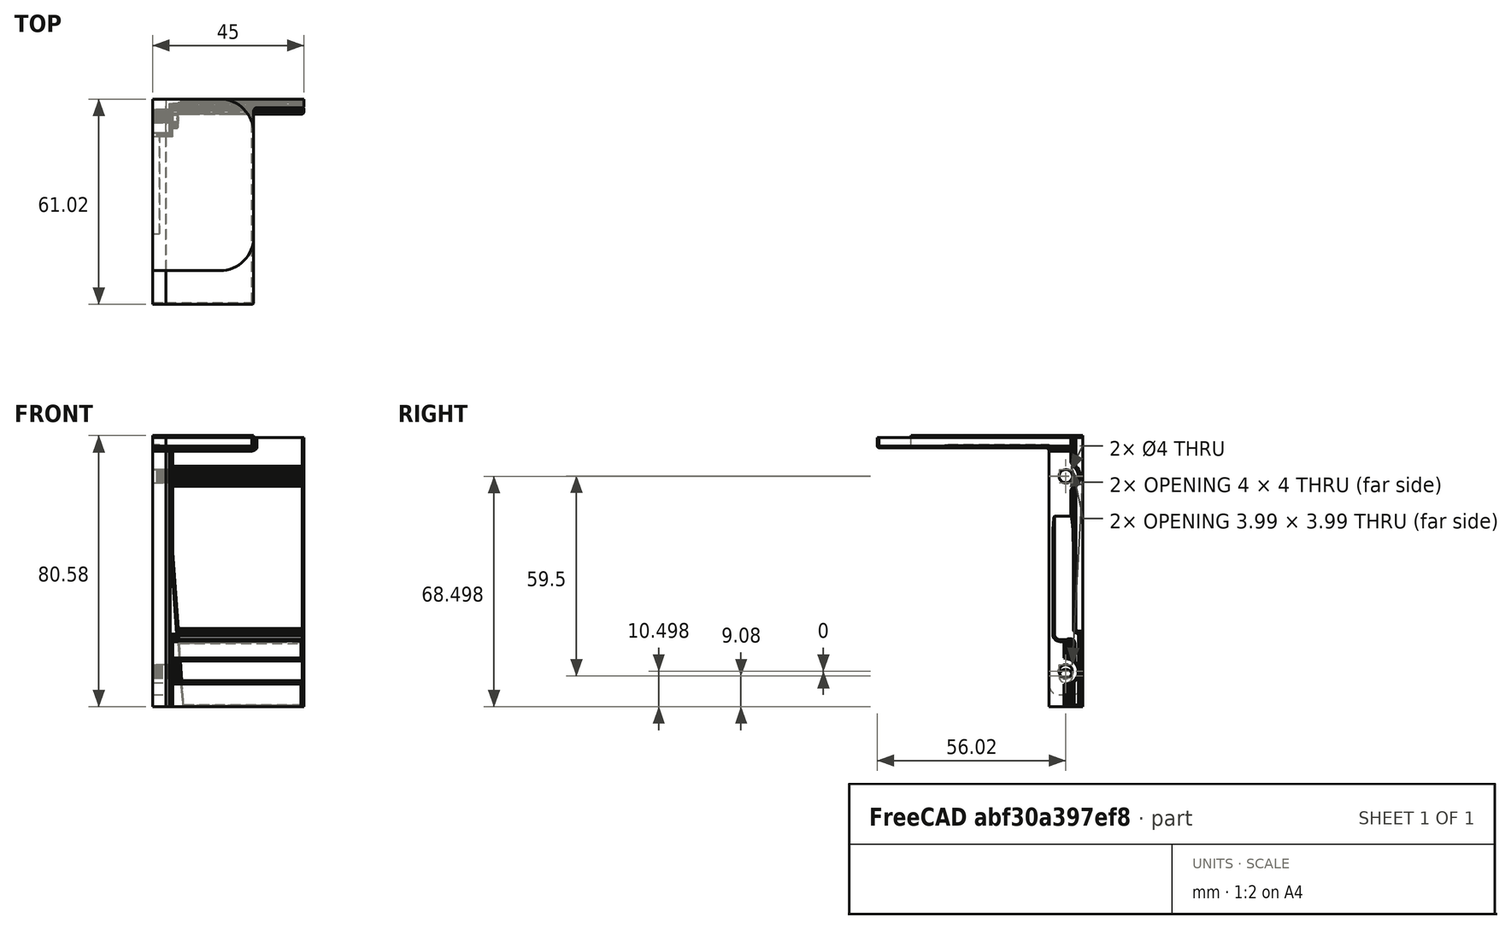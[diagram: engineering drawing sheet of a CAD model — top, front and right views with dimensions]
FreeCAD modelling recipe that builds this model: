
FCSTD DOCUMENT  (FreeCAD 0.19R)
Label: anycubic_max4pro_x_limit
License: All rights reserved
LicenseURL: http://en.wikipedia.org/wiki/All_rights_reserved
objects: Part::Feature×3, Part::FeaturePython×3, Part::Box×2, Part::Fillet×2, Part::Cylinder×2, Part::MultiFuse×2, App::Part×1, Mesh::Feature×1, Part::Refine×1, Part::Plane×1, App::DocumentObjectGroup×1, Part::Cut×1
note: 17 computed .brp shape members not serialized (recipe doc carries the construction recipe); baked Part::Feature solids carry a one-line shape summary decoded from their .brp

FEATURE [App::Part] Part
  Origin = -> Origin
FEATURE [Mesh::Feature] new_headlimit_maxpro_v5_v10
FEATURE [Part::Feature] new_headlimit_maxpro_v5_v10001
  shape: bbox 45 x 61.02 x 80 mm, 7914 faces, 0 solids (baked)
FEATURE [Part::Refine] new_headlimit_maxpro_v5_v10001001
  Source = -> new_headlimit_maxpro_v5_v10001
FEATURE [Part::Feature] new_headlimit_maxpro_v5_v10001001001
  shape: bbox 45 x 61.02 x 80 mm, 5194 faces, 0 solids (baked)
FEATURE [Part::Plane] Plane
  AttacherType = Attacher::AttachEngine3D
  Length = 100
  Placement = pos=(4,-65,6) rot=(0,1,0;1.5708rad)
  Width = 100
FEATURE [Part::Box] Box001  label="Cube001"
  AttacherType = Attacher::AttachEngine3D
  Height = 3
  Length = 30
  Placement = pos=(0,-41,-2) rot=(0,0,1;0rad)
  Width = 51
FEATURE [Part::Feature] new_headlimit_maxpro_v5_v10001001_solid  label="new_headlimit_maxpro_v5_v10001001 (Solid)"
  shape: bbox 45 x 61.02 x 80 mm, 5194 faces (baked)
FEATURE [Part::FeaturePython] Slice  # WARN: FeaturePython — macro-defined, semantics opaque (R4)
  Base = -> new_headlimit_maxpro_v5_v10001001_solid
  Mode = 1
  Tolerance = 0
  Tools = -> [Plane]
FEATURE [Part::FeaturePython] Slice_child0  label="Slice.0"  # WARN: FeaturePython — macro-defined, semantics opaque (R4)
  Base = -> Slice
  FilterType = 1
  Invert = false
  OverrideMaxVal = 0
  WindowFrom = 80
  WindowTo = 100
  items = 0
FEATURE [Part::FeaturePython] Slice_child1  label="Slice.1"  # WARN: FeaturePython — macro-defined, semantics opaque (R4)
  Base = -> Slice
  FilterType = 1
  Invert = false
  OverrideMaxVal = 0
  WindowFrom = 80
  WindowTo = 100
  items = 1
FEATURE [App::DocumentObjectGroup] GrExplode_Slice  label="Exploded Slice"
  Group = -> [Slice_child0,Slice_child1]
FEATURE [Part::Fillet] Fillet
  Base = -> Box001
  Edges = 2 edges r=10: [Edge5,Edge7]
FEATURE [Part::Cylinder] Cylinder
  Angle = 360
  AttacherType = Attacher::AttachEngine3D
  Height = 10
  Placement = pos=(4.7e-15,5,-70.5) rot=(0,1,0;1.5708rad)
  Radius = 2
FEATURE [Part::Cylinder] Cylinder001
  Angle = 360
  AttacherType = Attacher::AttachEngine3D
  Height = 10
  Placement = pos=(-8.3e-15,5,-11) rot=(0,1,0;1.5708rad)
  Radius = 2
FEATURE [Part::Box] Box  label="Cube"
  AttacherType = Attacher::AttachEngine3D
  Height = 76
  Length = 4
  Placement = pos=(0,0,-76) rot=(0,0,1;0rad)
  Width = 10
FEATURE [Part::Fillet] Fillet001
  Base = -> Box
  Edges = 2 edges r=3: [Edge9,Edge11]
FEATURE [Part::MultiFuse] Fusion  label="body fusion"
  Shapes = -> [Fillet,Fillet001]
FEATURE [Part::MultiFuse] Fusion001  label="hole fusion"
  Shapes = -> [Cylinder,Cylinder001]
FEATURE [Part::Cut] Cut  label="body cut"
  Base = -> Fusion
  Tool = -> Fusion001
